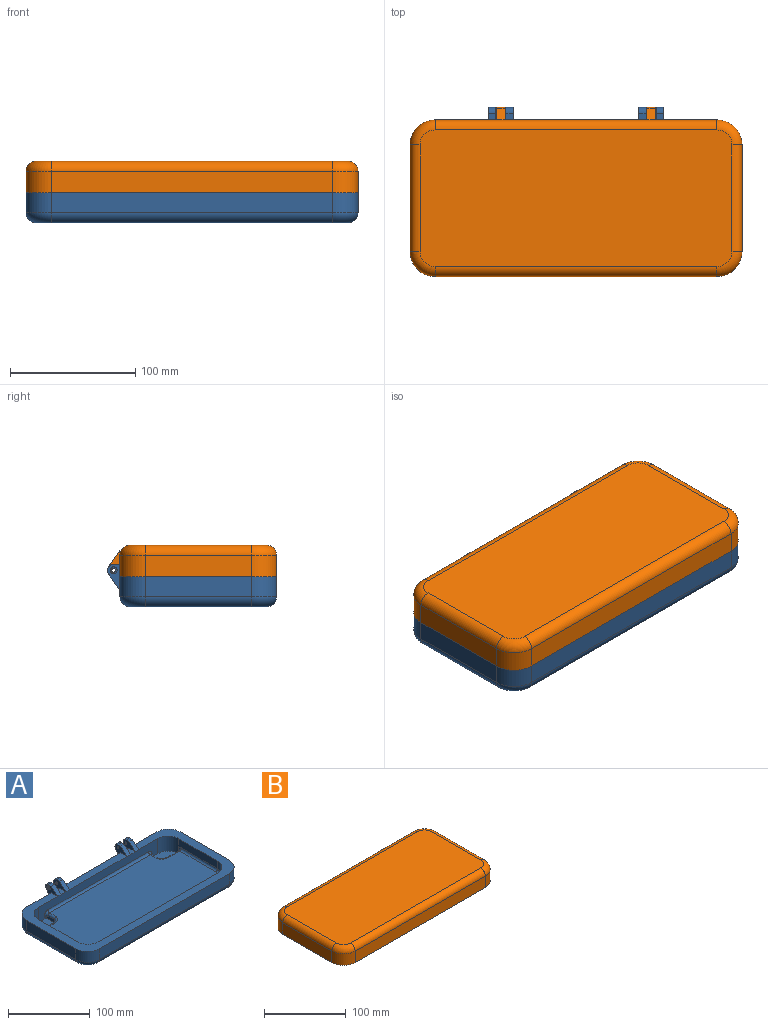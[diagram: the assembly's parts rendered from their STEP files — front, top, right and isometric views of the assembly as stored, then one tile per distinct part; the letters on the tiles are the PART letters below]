
ASSEMBLY  parts=2 mates=1
PART A: 92 faces, bbox 268.3x136.7x35.1 mm
  f0: plane 6x5mm, normal (0,0,1), area 30mm2, adj f1,f5,f88,f91
  f1: plane 11x10mm, normal (0,-0.67,0.74), area 89.2mm2, adj f0,f51,f88,f91
  f2: plane 10.89x6mm, normal (0,-1,0), area 65.3mm2, adj f3,f32,f88,f91
  f3: plane 13.03x9.08mm, normal (0,0.82,-0.57), area 95.3mm2, adj f2,f5,f88,f91
  f4: cylinder r=1.5mm len=6mm, axis (-1,0,0), area 56.5mm2, adj f88,f91
  f5: cylinder r=5mm len=7.86mm, axis (-1,0,0), area 65.4mm2, adj f0,f3,f88,f91
  f6: plane 11x8mm, normal (0,0,1), area 88mm2, adj f32,f51,f80,f88
  f7: plane 10.89x6mm, normal (0,-1,0), area 65.3mm2, adj f8,f32,f74,f80
  f8: plane 13.03x9.08mm, normal (0,0.82,-0.57), area 95.3mm2, adj f7,f11,f74,f80
  f9: plane 6x5mm, normal (0,0,1), area 30mm2, adj f10,f11,f74,f80
  f10: plane 11x10mm, normal (0,-0.67,0.74), area 89.2mm2, adj f9,f51,f74,f80
  f11: cylinder r=5mm len=7.86mm, axis (-1,0,0), area 65.4mm2, adj f8,f9,f74,f80
  f12: cylinder r=1.5mm len=4mm, axis (-1,0,0), area 37.7mm2, adj f77,f80
  f13: cylinder r=2.75mm len=5.5mm, axis (-1,0,0), area 34.6mm2, adj f74,f77
  f14: cylinder r=3mm len=62mm, axis (0,1,0), area 292.2mm2, adj f21,f22,f56,f60
  f15: cylinder r=3mm len=62mm, axis (0,-1,0), area 292.2mm2, adj f18,f23,f56,f57
  f16: cylinder r=3mm len=19mm, axis (1,0,0), area 89.5mm2, adj f18,f27,f56,f59
  f17: cylinder r=3mm len=19mm, axis (1,0,0), area 89.5mm2, adj f21,f26,f56,f65
  f18: torus R=6mm, axis (1,0,0), area 42.3mm2, adj f15,f16,f19,f23,f27,f50,f52
  f19: cylinder r=18mm len=22.5mm, axis (0,0,1), area 633mm2, adj f18,f23,f30,f50,f51,f52
  f20: cylinder r=18mm len=22.5mm, axis (0,0,1), area 633mm2, adj f21,f22,f30,f48,f49,f51
  f21: torus R=6mm, axis (1,0,0), area 42.3mm2, adj f14,f17,f20,f22,f26,f48,f49
  f22: plane 67x14.18mm, normal (-1,0,0), area 774.5mm2, adj f14,f20,f21,f30,f55
  f23: plane 67x14.18mm, normal (1,0,0), area 774.5mm2, adj f15,f18,f19,f30,f53
  f24: plane 14.35x5mm, normal (1,0,0), area 66.4mm2, adj f25,f49,f64,f66
  f25: cylinder r=10mm len=9mm, axis (0,0,1), area 56mm2, adj f24,f26,f49,f65
  f26: plane 22x5mm, normal (0,1,0), area 104.6mm2, adj f17,f21,f25,f49
  f27: plane 22x5mm, normal (0,1,0), area 104.6mm2, adj f16,f18,f28,f52
  f28: cylinder r=10mm len=9mm, axis (0,0,1), area 56mm2, adj f27,f29,f52,f59
  f29: plane 14.35x5mm, normal (-1,0,0), area 66.4mm2, adj f28,f52,f61,f62
  f30: plane 265x125mm, normal (0,0,1), area 6593.8mm2, adj f19,f20,f22,f23,f31,f32,f33,f34
  f31: cylinder r=20mm len=20mm, axis (0,0,1), area 502.7mm2, adj f30,f32,f38,f44
  f32: plane 225x16mm, normal (0,1,0), area 3600mm2, adj f2,f6,f7,f30,f31,f33,f42,f67
  f33: cylinder r=20mm len=20mm, axis (0,0,1), area 502.7mm2, adj f30,f32,f34,f40
  f34: plane 85x16mm, normal (-1,0,0), area 1360mm2, adj f30,f33,f35,f41
  f35: cylinder r=20mm len=20mm, axis (0,0,1), area 502.7mm2, adj f30,f34,f36,f43
  f36: plane 225x16mm, normal (0,-1,0), area 3600mm2, adj f30,f35,f37,f45
  f37: cylinder r=20mm len=20mm, axis (0,0,1), area 502.7mm2, adj f30,f36,f38,f47
  f38: plane 85x16mm, normal (1,0,0), area 1360mm2, adj f30,f31,f37,f46
  f39: plane 249x109mm, normal (0,0,-1), area 27017.4mm2, adj f40,f41,f42,f43,f44,f45,f46,f47
  f40: torus R=12mm, axis (0,0,1), area 337.4mm2, adj f33,f39,f41,f42
  f41: cylinder r=8mm len=85mm, axis (0,1,0), area 1068.1mm2, adj f34,f39,f40,f43
  f42: cylinder r=8mm len=225mm, axis (1,0,0), area 2827.4mm2, adj f32,f39,f40,f44
  f43: torus R=12mm, axis (0,0,1), area 337.4mm2, adj f35,f39,f41,f45
  f44: torus R=12mm, axis (0,0,1), area 337.4mm2, adj f31,f39,f42,f46
  f45: cylinder r=8mm len=225mm, axis (-1,0,0), area 2827.4mm2, adj f36,f39,f43,f47
  f46: cylinder r=8mm len=85mm, axis (0,-1,0), area 1068.1mm2, adj f38,f39,f44,f47
  f47: torus R=12mm, axis (0,0,1), area 337.4mm2, adj f37,f39,f45,f46
  f48: plane 1.68x1.68mm, normal (-1,0,0), area 1.2mm2, adj f20,f21,f49
  f49: plane 31x20mm, normal (0,0,1), area 536.1mm2, adj f20,f21,f24,f25,f26,f48,f51,f64
  f50: plane 1.68x1.68mm, normal (1,0,0), area 1.2mm2, adj f18,f19,f52
  f51: plane 206x22.5mm, normal (0,-1,0), area 2612.4mm2, adj f1,f6,f10,f19,f20,f30,f49,f52
  f52: plane 31x20mm, normal (0,0,1), area 536.1mm2, adj f18,f19,f27,f28,f29,f50,f51,f62
  f53: cylinder r=18mm len=18mm, axis (0,0,1), area 325.2mm2, adj f23,f30,f54,f57
  f54: plane 206x11.5mm, normal (0,1,0), area 2369mm2, adj f30,f53,f55,f58
  f55: cylinder r=18mm len=18mm, axis (0,0,1), area 325.2mm2, adj f22,f30,f54,f60
  f56: plane 236x97mm, normal (0,0,1), area 21608.7mm2, adj f14,f15,f16,f17,f57,f58,f59,f60
  f57: torus R=15mm, axis (0,0,1), area 125.2mm2, adj f15,f53,f56,f58
  f58: cylinder r=3mm len=206mm, axis (1,0,0), area 970.8mm2, adj f54,f56,f57,f60
  f59: torus R=13mm, axis (0,0,1), area 60.1mm2, adj f16,f28,f56,f61
  f60: torus R=15mm, axis (0,0,1), area 125.2mm2, adj f14,f55,f56,f58
  f61: cylinder r=3mm len=12mm, axis (0,1,0), area 54.7mm2, adj f29,f56,f59,f62
  f62: torus R=6mm, axis (0,1,0), area 43.6mm2, adj f29,f51,f52,f61,f63
  f63: cylinder r=3mm len=174mm, axis (-1,0,0), area 820mm2, adj f51,f56,f62,f64
  f64: torus R=6mm, axis (0,1,0), area 43.6mm2, adj f24,f49,f51,f63,f66
  f65: torus R=13mm, axis (0,0,1), area 60.1mm2, adj f17,f25,f56,f66
  f66: cylinder r=3mm len=12mm, axis (0,-1,0), area 54.7mm2, adj f24,f56,f64,f65
  f67: plane 10.89x6mm, normal (0,-1,0), area 65.3mm2, adj f32,f68,f73,f79
  f68: plane 13.03x9.08mm, normal (0,0.82,-0.57), area 95.3mm2, adj f67,f69,f73,f79
  f69: cylinder r=5mm len=7.86mm, axis (-1,0,0), area 65.4mm2, adj f68,f70,f73,f79
  f70: plane 6x5mm, normal (0,0,1), area 30mm2, adj f69,f71,f73,f79
  f71: plane 11x10mm, normal (0,-0.67,0.74), area 89.2mm2, adj f51,f70,f73,f79
  f72: cylinder r=2.75mm len=5.5mm, axis (-1,0,0), area 34.6mm2, adj f73,f76
  f73: plane 21x20.89mm, normal (1,0,0), area 163mm2, adj f30,f67,f68,f69,f70,f71,f72
  f74: plane 21x20.89mm, normal (-1,0,0), area 163mm2, adj f7,f8,f9,f10,f11,f13,f30
  f75: cylinder r=1.5mm len=4mm, axis (-1,0,0), area 37.7mm2, adj f76,f79
  f76: plane 5.5x5.5mm, normal (1,0,0), area 16.7mm2, adj f72,f75
  f77: plane 5.5x5.5mm, normal (-1,0,0), area 16.7mm2, adj f12,f13
  f78: plane 11x8mm, normal (0,0,1), area 88mm2, adj f32,f51,f79,f87
  f79: plane 21x20.89mm, normal (-1,0,0), area 179.6mm2, adj f67,f68,f69,f70,f71,f75,f78
  f80: plane 21x20.89mm, normal (1,0,0), area 179.6mm2, adj f6,f7,f8,f9,f10,f11,f12
  f81: cylinder r=5mm len=7.86mm, axis (-1,0,0), area 65.4mm2, adj f82,f85,f87,f90
  f82: plane 6x5mm, normal (0,0,1), area 30mm2, adj f81,f83,f87,f90
  f83: plane 11x10mm, normal (0,-0.67,0.74), area 89.2mm2, adj f51,f82,f87,f90
  f84: plane 10.89x6mm, normal (0,-1,0), area 65.3mm2, adj f32,f85,f87,f90
  f85: plane 13.03x9.08mm, normal (0,0.82,-0.57), area 95.3mm2, adj f81,f84,f87,f90
  f86: cylinder r=1.5mm len=6mm, axis (-1,0,0), area 56.5mm2, adj f87,f90
  f87: plane 21x20.89mm, normal (1,0,0), area 179.6mm2, adj f78,f81,f82,f83,f84,f85,f86
  f88: plane 21x20.89mm, normal (-1,0,0), area 179.6mm2, adj f0,f1,f2,f3,f4,f5,f6
  f89: plane 100x11mm, normal (0,0,1), area 1100mm2, adj f32,f51,f90,f91
  f90: plane 21x20.89mm, normal (-1,0,0), area 179.6mm2, adj f81,f82,f83,f84,f85,f86,f89
  f91: plane 21x20.89mm, normal (1,0,0), area 179.6mm2, adj f0,f1,f2,f3,f4,f5,f89
PART B: 60 faces, bbox 268.3x136.6x25 mm
  f0: plane 16x7mm, normal (0,0,-1), area 112mm2, adj f31,f35,f39,f45
  f1: plane 99x11mm, normal (0,0,-1), area 1089mm2, adj f37,f41,f42,f45
  f2: plane 16x7mm, normal (0,0,-1), area 112mm2, adj f7,f36,f40,f45
  f3: plane 265x125mm, normal (0,0,-1), area 6582.8mm2, adj f10,f11,f12,f13,f14,f15,f16,f17
  f4: plane 11x10mm, normal (0,0.67,-0.74), area 104.1mm2, adj f37,f40,f42,f45
  f5: plane 12.99x9.1mm, normal (0,0.82,0.57), area 111mm2, adj f6,f7,f36,f40
  f6: plane 7x3.86mm, normal (0,-1,0), area 27mm2, adj f5,f22,f36,f40
  f7: cylinder r=5mm len=7.87mm, axis (-1,0,0), area 76.4mm2, adj f2,f5,f36,f40
  f8: cylinder r=1.5mm len=7mm, axis (-1,0,0), area 66mm2, adj f36,f40
  f9: plane 11x10mm, normal (0,0.67,-0.74), area 104.1mm2, adj f10,f30,f36,f45
  f10: plane 49x17mm, normal (0,1,0), area 763mm2, adj f3,f9,f13,f22,f30,f36
  f11: plane 49x17mm, normal (0,1,0), area 763mm2, adj f3,f12,f22,f28,f29,f35
  f12: cylinder r=20mm len=20mm, axis (0,0,-1), area 534.1mm2, adj f3,f11,f18,f24
  f13: cylinder r=20mm len=20mm, axis (0,0,-1), area 534.1mm2, adj f3,f10,f14,f20
  f14: plane 85x17mm, normal (-1,0,0), area 1445mm2, adj f3,f13,f15,f21
  f15: cylinder r=20mm len=20mm, axis (0,0,-1), area 534.1mm2, adj f3,f14,f16,f23
  f16: plane 225x17mm, normal (0,-1,0), area 3825mm2, adj f3,f15,f17,f25
  f17: cylinder r=20mm len=20mm, axis (0,0,-1), area 534.1mm2, adj f3,f16,f18,f27
  f18: plane 85x17mm, normal (1,0,0), area 1445mm2, adj f3,f12,f17,f26
  f19: plane 249x109mm, normal (0,0,1), area 27017.4mm2, adj f20,f21,f22,f23,f24,f25,f26,f27
  f20: torus R=12mm, axis (0,0,1), area 337.4mm2, adj f13,f19,f21,f22
  f21: cylinder r=8mm len=85mm, axis (0,1,0), area 1068.1mm2, adj f14,f19,f20,f23
  f22: cylinder r=8mm len=225mm, axis (1,0,0), area 2827.4mm2, adj f6,f10,f11,f19,f20,f24,f33,f37
  f23: torus R=12mm, axis (0,0,1), area 337.4mm2, adj f15,f19,f21,f25
  f24: torus R=12mm, axis (0,0,1), area 337.4mm2, adj f12,f19,f22,f26
  f25: cylinder r=8mm len=225mm, axis (-1,0,0), area 2827.4mm2, adj f16,f19,f23,f27
  f26: cylinder r=8mm len=85mm, axis (0,-1,0), area 1068.1mm2, adj f18,f19,f24,f27
  f27: torus R=12mm, axis (0,0,1), area 337.4mm2, adj f17,f19,f25,f26
  f28: plane 11x10mm, normal (0,0.67,-0.74), area 104.1mm2, adj f11,f29,f35,f45
  f29: plane 11x10mm, normal (-1,0,0), area 55mm2, adj f3,f11,f28
  f30: plane 11x10mm, normal (1,0,0), area 55mm2, adj f3,f9,f10
  f31: cylinder r=5mm len=7.87mm, axis (-1,0,0), area 76.4mm2, adj f0,f32,f35,f39
  f32: plane 12.99x9.1mm, normal (0,0.82,0.57), area 111mm2, adj f31,f33,f35,f39
  f33: plane 7x3.86mm, normal (0,-1,0), area 27mm2, adj f22,f32,f35,f39
  f34: cylinder r=1.5mm len=7mm, axis (-1,0,0), area 66mm2, adj f35,f39
  f35: plane 21x20.86mm, normal (1,0,0), area 179.5mm2, adj f0,f11,f28,f31,f32,f33,f34
  f36: plane 21x20.86mm, normal (-1,0,0), area 179.5mm2, adj f2,f5,f6,f7,f8,f9,f10
  f37: plane 113x17mm, normal (0,1,0), area 1781mm2, adj f1,f4,f22,f38,f39,f40,f41,f42
  f38: plane 11x10mm, normal (0,0.67,-0.74), area 104.1mm2, adj f37,f39,f41,f45
  f39: plane 21x20.86mm, normal (-1,0,0), area 179.5mm2, adj f0,f31,f32,f33,f34,f37,f38
  f40: plane 21x20.86mm, normal (1,0,0), area 179.5mm2, adj f2,f4,f5,f6,f7,f8,f37
  f41: plane 11x10mm, normal (1,0,0), area 55mm2, adj f1,f37,f38
  f42: plane 11x10mm, normal (-1,0,0), area 55mm2, adj f1,f4,f37
  f43: plane 67x19.5mm, normal (-1,0,0), area 1306.5mm2, adj f3,f44,f50,f53
  f44: cylinder r=18mm len=19.5mm, axis (0,0,-1), area 551.3mm2, adj f3,f43,f45,f55
  f45: plane 206x19.5mm, normal (0,-1,0), area 4017mm2, adj f0,f1,f2,f3,f4,f9,f28,f38
  f46: cylinder r=18mm len=19.5mm, axis (0,0,-1), area 551.3mm2, adj f3,f45,f47,f59
  f47: plane 67x19.5mm, normal (1,0,0), area 1306.5mm2, adj f3,f46,f48,f58
  f48: cylinder r=18mm len=19.5mm, axis (0,0,-1), area 551.3mm2, adj f3,f47,f49,f56
  f49: plane 206x19.5mm, normal (0,1,0), area 4017mm2, adj f3,f48,f50,f54
  f50: cylinder r=18mm len=19.5mm, axis (0,0,-1), area 551.3mm2, adj f3,f43,f49,f52
  f51: plane 236x97mm, normal (0,0,-1), area 22698.9mm2, adj f52,f53,f54,f55,f56,f57,f58,f59
  f52: torus R=15mm, axis (0,0,1), area 125.2mm2, adj f50,f51,f53,f54
  f53: cylinder r=3mm len=67mm, axis (0,1,0), area 315.7mm2, adj f43,f51,f52,f55
  f54: cylinder r=3mm len=206mm, axis (1,0,0), area 970.8mm2, adj f49,f51,f52,f56
  f55: torus R=15mm, axis (0,0,1), area 125.2mm2, adj f44,f51,f53,f57
  f56: torus R=15mm, axis (0,0,1), area 125.2mm2, adj f48,f51,f54,f58
  f57: cylinder r=3mm len=206mm, axis (-1,0,0), area 970.8mm2, adj f45,f51,f55,f59
  f58: cylinder r=3mm len=67mm, axis (0,-1,0), area 315.7mm2, adj f47,f51,f56,f59
  f59: torus R=15mm, axis (0,0,1), area 125.2mm2, adj f46,f51,f57,f58
PLACE A at identity
PLACE B rot(axis=(1,0,0),0deg) t=(0,0,0)mm
MATE pin_slot B.f7 <-> A.f4  axis (-1,0,0) through (56.5,67.5,5)mm
